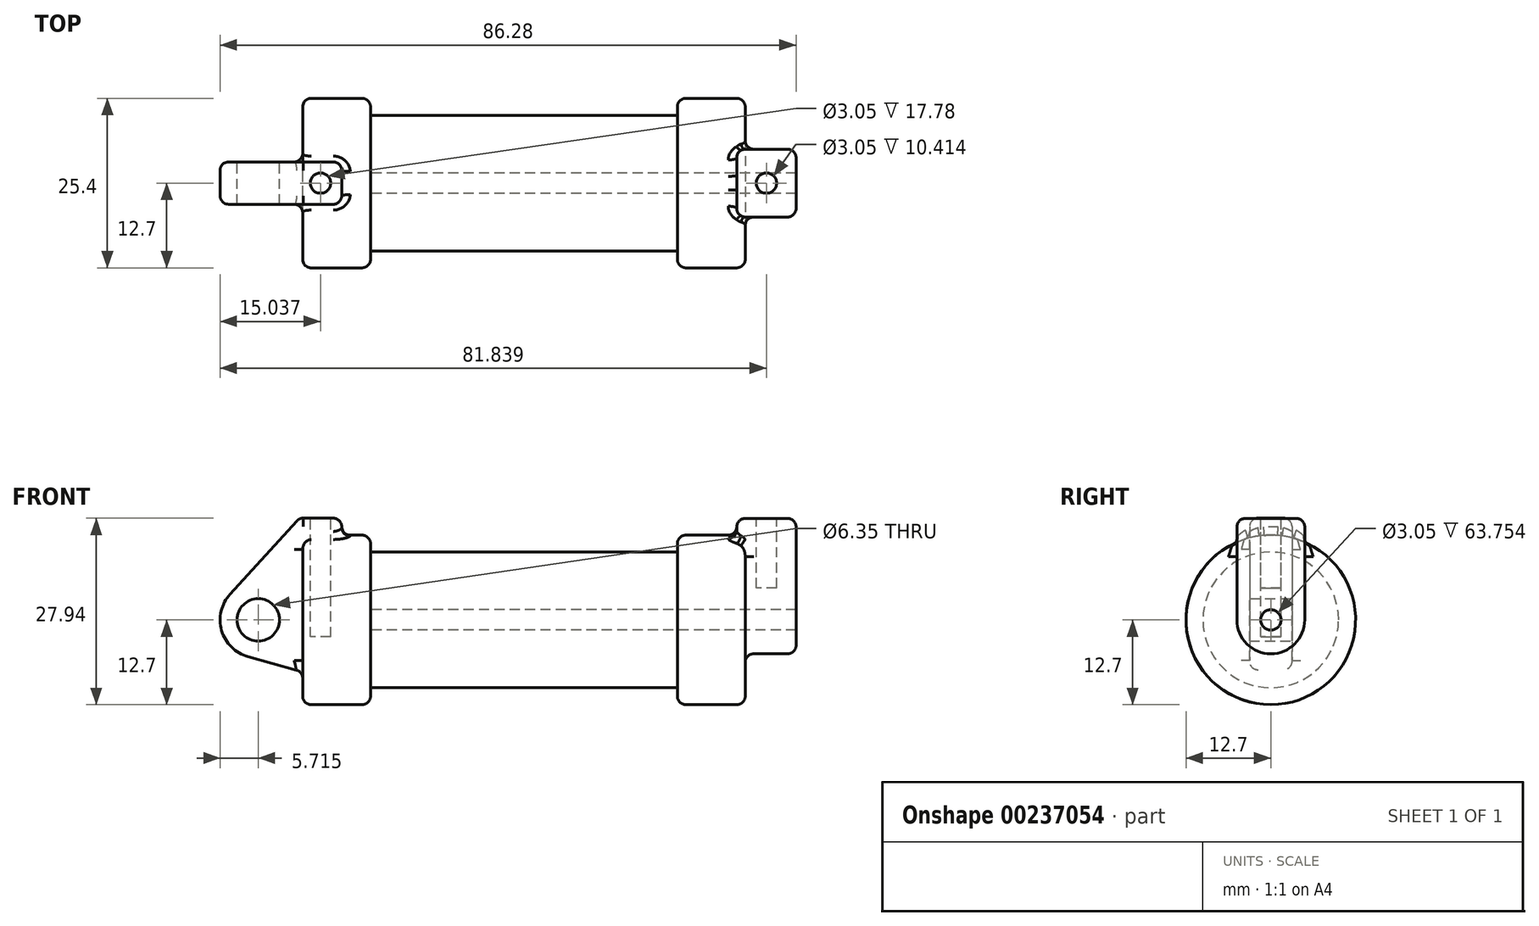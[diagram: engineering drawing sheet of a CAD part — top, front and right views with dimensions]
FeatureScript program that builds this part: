
annotation { "Feature Type Name" : "Feature", "Feature Type Description" : "" }
export const myFeature = defineFeature(function(context is Context, id is Id, definition is map)
    precondition{}
    {
        {
            var Q0;
            Q0=qCreatedBy(makeId("Front.planeOp"),FACE);
            var sketch = newSketch(context, id + "F0", { "sketchPlane" : qUnion([Q0])});
            skLineSegment(sketch, "E0", {"start": v(0, 0) * mm, "end": v(0, 12.7) * mm});
            skLineSegment(sketch, "E1", {"start": v(0, 12.7) * mm, "end": v(10.16, 12.7) * mm});
            skLineSegment(sketch, "E2", {"start": v(10.16, 12.7) * mm, "end": v(10.16, 10.16) * mm});
            skLineSegment(sketch, "E3", {"start": v(10.16, 10.16) * mm, "end": v(56.13, 10.16) * mm});
            skLineSegment(sketch, "E4", {"start": v(56.13, 10.16) * mm, "end": v(56.13, 12.7) * mm});
            skLineSegment(sketch, "E5", {"start": v(56.13, 12.7) * mm, "end": v(66.3, 12.7) * mm});
            skLineSegment(sketch, "E6", {"start": v(66.3, 12.7) * mm, "end": v(66.3, 0) * mm});
            skLineSegment(sketch, "E7", {"start": v(66.3, 0) * mm, "end": v(0, 0) * mm});
            skLineSegment(sketch, "E8", {"start": v(5.84, 15.24) * mm, "end": v(-0.5, 15.24) * mm});
            skLineSegment(sketch, "E9", {"start": v(-0.5, 15.24) * mm, "end": v(-10.88, 3.85) * mm});
            skLineSegment(sketch, "E10", {"start": v(0, 0) * mm, "end": v(-6.65, 0) * mm});
            skCircle(sketch, "E11", {"center": v(-6.65, 0) * mm, "radius": 5.72 * mm});
            skCircle(sketch, "E12", {"center": v(-6.65, 0) * mm, "radius": 3.18 * mm});
            skLineSegment(sketch, "E13", {"start": v(5.84, 15.24) * mm, "end": v(5.84, -9.4) * mm});
            skLineSegment(sketch, "E14", {"start": v(5.84, -9.4) * mm, "end": v(-8.18, -5.5) * mm});
            skSolve(sketch);
        }
        {
            var Q0;
            {var subQ0=sQuery(id+"F0.wireOp",EDGE,"E2");Q0=makeQuery(id+"F0.imprint","IMPRINT",FACE,{"disambiguationData":[TD([[makeQuery(id+"F0.imprint","IMPRINT",EDGE,{"derivedFrom":subQ0}),-1.0]])]});}
            var Q1;
            {var subQ0=sQuery(id+"F0.wireOp",EDGE,"E0");Q1=makeQuery(id+"F0.imprint","IMPRINT",FACE,{"disambiguationData":[TD([[makeQuery(id+"F0.imprint","IMPRINT",EDGE,{"derivedFrom":subQ0}),-1.0]])]});}
            var Q2;
            Q2=sQuery(id+"F0.wireOp",EDGE,"E7");
            revolve(context, id + "F1", {"entities" : qUnion([Q0, Q1]), "axis" : qUnion([Q2]), "revolveType" : RevolveType.FULL});
        }
        {
            var Q0;
            {var subQ0=sQuery(id+"F0.wireOp",EDGE,"E0");Q0=makeQuery(id+"F0.imprint","IMPRINT",FACE,{"disambiguationData":[TD([[makeQuery(id+"F0.imprint","IMPRINT",EDGE,{"derivedFrom":subQ0}),-1.0]])]});}
            var Q1;
            {var subQ3=sQuery(id+"F0.wireOp",EDGE,"E0");Q1=makeQuery(id+"F0.imprint","IMPRINT",FACE,{"disambiguationData":[TD([[makeQuery(id+"F0.imprint","IMPRINT",EDGE,{"derivedFrom":subQ3}),1.0]])]});}
            var Q2;
            {var subQ0=sQuery(id+"F0.wireOp",EDGE,"E14");Q2=makeQuery(id+"F0.imprint","IMPRINT",FACE,{"disambiguationData":[TD([[makeQuery(id+"F0.imprint","IMPRINT",EDGE,{"derivedFrom":subQ0}),-1.0]])]});}
            var Q3;
            {var subQ4=sQuery(id+"F0.wireOp",EDGE,"E12");Q3=makeQuery(id+"F0.imprint","IMPRINT",FACE,{"disambiguationData":[TD([[makeQuery(id+"F0.imprint","IMPRINT",EDGE,{"derivedFrom":subQ4}),-1.0]])]});}
            extrude(context, id + "F2", {"entities" : qUnion([Q0, Q1, Q2, Q3]), "operationType" : NewBodyOperationType.ADD, "endBound" : BoundingType.SYMMETRIC, "depth" : 6.35 * mm});
        }
        {
            var Q0;
            Q0=makeQuery(id+"F1.opRevolve","SWEPT_FACE",FACE,{"disambiguationData":[OSD([sQuery(id+"F0.wireOp",EDGE,"E6")])]});
            var sketch = newSketch(context, id + "F3", { "sketchPlane" : qUnion([Q0])});
            skCircle(sketch, "E15", {"center": v(0, 0) * mm, "radius": 1.52 * mm});
            skCircle(sketch, "E16", {"center": v(0, 0) * mm, "radius": 5.08 * mm});
            skLineSegment(sketch, "E17", {"start": v(5.08, 0) * mm, "end": v(5.08, 15.2) * mm});
            skLineSegment(sketch, "E18", {"start": v(-5.08, 0) * mm, "end": v(-5.08, 15.2) * mm});
            skLineSegment(sketch, "E19", {"start": v(-5.08, 15.2) * mm, "end": v(5.08, 15.2) * mm});
            skSolve(sketch);
        }
        {
            var Q0;
            Q0 = qSketchRegion(id + "F3", true);
            extrude(context, id + "F4", {"entities" : qUnion([Q0]), "operationType" : NewBodyOperationType.ADD, "depth" : 7.62 * mm, "hasSecondDirection" : true, "secondDirectionOppositeDirection" : true, "secondDirectionDepth" : 1.27 * mm});
        }
        {
            var Q0;
            Q0=makeQuery(id+"F4.boolean.opBoolean","SPLIT",FACE,{"disambiguationData":[TD([makeQuery(id+"F4.opExtrude","SWEPT_FACE",FACE,{"disambiguationData":[OSD([sQuery(id+"F3.wireOp",EDGE,"E15")])]})])],"derivedFrom":makeQuery(id+"F1.opRevolve","SWEPT_FACE",FACE,{"disambiguationData":[OSD([sQuery(id+"F0.wireOp",EDGE,"E6")])]})});
            var Q1;
            Q1=makeQuery(id+"F1.opRevolve","SWEPT_FACE",FACE,{"disambiguationData":[OSD([sQuery(id+"F0.wireOp",EDGE,"E2")])]});
            extrude(context, id + "F5", {"entities" : qUnion([Q0]), "operationType" : NewBodyOperationType.REMOVE, "endBound" : BoundingType.UP_TO_SURFACE, "oppositeDirection" : true, "endBoundEntityFace" : qUnion([Q1]), "depth" : 25.4 * mm});
        }
        {
            var Q0;
            Q0=makeQuery(id+"F4.opExtrude","SWEPT_FACE",FACE,{"disambiguationData":[OSD([sQuery(id+"F3.wireOp",EDGE,"E19")])]});
            var sketch = newSketch(context, id + "F6", { "sketchPlane" : qUnion([Q0])});
            skCircle(sketch, "E20", {"center": v(69.47, 0) * mm, "radius": 1.52 * mm});
            skSolve(sketch);
        }
        {
            var Q0;
            Q0=makeQuery(id+"F2.opExtrude","SWEPT_FACE",FACE,{"disambiguationData":[OSD([sQuery(id+"F0.wireOp",EDGE,"E8")])]});
            var sketch = newSketch(context, id + "F7", { "sketchPlane" : qUnion([Q0])});
            skCircle(sketch, "E21", {"center": v(2.67, 0) * mm, "radius": 1.52 * mm});
            skSolve(sketch);
        }
        {
            var Q0;
            Q0 = qSketchRegion(id + "F7", true);
            extrude(context, id + "F8", {"entities" : qUnion([Q0]), "operationType" : NewBodyOperationType.REMOVE, "oppositeDirection" : true, "depth" : 17.78 * mm});
        }
        {
            var Q0;
            Q0 = qSketchRegion(id + "F6", true);
            extrude(context, id + "F9", {"entities" : qUnion([Q0]), "operationType" : NewBodyOperationType.REMOVE, "oppositeDirection" : true, "depth" : 10.4 * mm});
        }
        {
            var Q0;
            Q0=makeQuery(id+"F1.opRevolve","SWEPT_EDGE",EDGE,{"disambiguationData":[OSD([sQuery(id+"F0.wireOp",EDGE,"E1"),sQuery(id+"F0.wireOp",EDGE,"E2")])]});
            fillet(context, id + "F10", {"entities" : qUnion([Q0]), "radius" : 1.27 * mm, "tangentPropagation" : true, "allowEdgeOverflow" : false});
        }
        {
            var Q0;
            Q0=makeQuery(id+"F1.opRevolve","SWEPT_EDGE",EDGE,{"disambiguationData":[OSD([sQuery(id+"F0.wireOp",EDGE,"E0"),sQuery(id+"F0.wireOp",EDGE,"E1")])]});
            fillet(context, id + "F11", {"entities" : qUnion([Q0]), "radius" : 1.27 * mm, "tangentPropagation" : true, "allowEdgeOverflow" : false});
        }
        {
            var Q0;
            Q0=makeQuery(id+"F1.opRevolve","SWEPT_EDGE",EDGE,{"disambiguationData":[OSD([sQuery(id+"F0.wireOp",EDGE,"E4"),sQuery(id+"F0.wireOp",EDGE,"E5")])]});
            fillet(context, id + "F12", {"entities" : qUnion([Q0]), "radius" : 1.27 * mm, "tangentPropagation" : true, "allowEdgeOverflow" : false});
        }
        {
            var Q0;
            Q0=makeQuery(id+"F1.opRevolve","SWEPT_EDGE",EDGE,{"disambiguationData":[OSD([sQuery(id+"F0.wireOp",EDGE,"E5"),sQuery(id+"F0.wireOp",EDGE,"E6")])]});
            fillet(context, id + "F13", {"entities" : qUnion([Q0]), "radius" : 1.27 * mm, "tangentPropagation" : true, "allowEdgeOverflow" : false});
        }
        {
            var Q0;
            Q0=makeQuery(id+"F2.opExtrude","SWEPT_EDGE",EDGE,{"disambiguationData":[OSD([sQuery(id+"F0.wireOp",EDGE,"E8"),sQuery(id+"F0.wireOp",EDGE,"E13")])]});
            fillet(context, id + "F14", {"entities" : qUnion([Q0]), "radius" : 1.27 * mm, "tangentPropagation" : true, "allowEdgeOverflow" : false});
        }
        {
            var Q0;
            Q0=makeQuery(id+"F2.opExtrude","CAP_EDGE",EDGE,{"disambiguationData":[OSD([sQuery(id+"F0.wireOp",EDGE,"E8")])],"isStart":false});
            fillet(context, id + "F15", {"entities" : qUnion([Q0]), "radius" : 1.27 * mm, "tangentPropagation" : true, "allowEdgeOverflow" : false});
        }
        {
            var Q0;
            Q0=makeQuery(id+"F2.opExtrude","CAP_EDGE",EDGE,{"disambiguationData":[OSD([sQuery(id+"F0.wireOp",EDGE,"E8")])],"isStart":true});
            fillet(context, id + "F16", {"entities" : qUnion([Q0]), "radius" : 1.27 * mm, "tangentPropagation" : true, "allowEdgeOverflow" : false});
        }
        {
            var Q0;
            Q0=makeQuery(id+"F2.opExtrude","CAP_EDGE",EDGE,{"disambiguationData":[OSD([sQuery(id+"F0.wireOp",EDGE,"E9")])],"isStart":true});
            fillet(context, id + "F17", {"entities" : qUnion([Q0]), "radius" : 1.27 * mm, "tangentPropagation" : true, "allowEdgeOverflow" : false});
        }
        {
            var Q0;
            Q0=makeQuery(id+"F2.boolean.opBoolean","INTERSECT",EDGE,{"derivedFrom":[makeQuery(id+"F1.opRevolve","SWEPT_FACE",FACE,{"disambiguationData":[OSD([sQuery(id+"F0.wireOp",EDGE,"E0")])]}),makeQuery(id+"F2.opExtrude","CAP_FACE",FACE,{"disambiguationData":[OSD([sQuery(id+"F0.wireOp",EDGE,"E8"),sQuery(id+"F0.wireOp",EDGE,"E9"),sQuery(id+"F0.wireOp",EDGE,"E11"),sQuery(id+"F0.wireOp",EDGE,"E12"),sQuery(id+"F0.wireOp",EDGE,"E13"),sQuery(id+"F0.wireOp",EDGE,"E14")])],"isStart":false})]});
            fillet(context, id + "F18", {"entities" : qUnion([Q0]), "radius" : 1.27 * mm, "tangentPropagation" : true, "allowEdgeOverflow" : false});
        }
        {
            var Q0;
            Q0=makeQuery(id+"F4.opExtrude","CAP_EDGE",EDGE,{"disambiguationData":[OSD([sQuery(id+"F3.wireOp",EDGE,"E18")])],"isStart":false});
            fillet(context, id + "F19", {"entities" : qUnion([Q0]), "radius" : 1.27 * mm, "tangentPropagation" : true, "allowEdgeOverflow" : false});
        }
        {
            var Q0;
            Q0=makeQuery(id+"F4.opExtrude","SWEPT_EDGE",EDGE,{"disambiguationData":[OSD([sQuery(id+"F3.wireOp",EDGE,"E18"),sQuery(id+"F3.wireOp",EDGE,"E19")])]});
            fillet(context, id + "F20", {"entities" : qUnion([Q0]), "radius" : 1.27 * mm, "tangentPropagation" : true, "allowEdgeOverflow" : false});
        }
        {
            var Q0;
            Q0=makeQuery(id+"F4.opExtrude","CAP_EDGE",EDGE,{"disambiguationData":[OSD([sQuery(id+"F3.wireOp",EDGE,"E19")])],"isStart":true});
            fillet(context, id + "F21", {"entities" : qUnion([Q0]), "radius" : 1.27 * mm, "tangentPropagation" : true, "allowEdgeOverflow" : false});
        }
        {
            var Q0;
            Q0=makeQuery(id+"F4.boolean.opBoolean","INTERSECT",EDGE,{"derivedFrom":[makeQuery(id+"F1.opRevolve","SWEPT_FACE",FACE,{"disambiguationData":[OSD([sQuery(id+"F0.wireOp",EDGE,"E6")])]}),makeQuery(id+"F4.opExtrude","SWEPT_FACE",FACE,{"disambiguationData":[OSD([sQuery(id+"F3.wireOp",EDGE,"E18")])]})]});
            fillet(context, id + "F22", {"entities" : qUnion([Q0]), "radius" : 1.27 * mm, "tangentPropagation" : true, "allowEdgeOverflow" : false});
        }
    });
